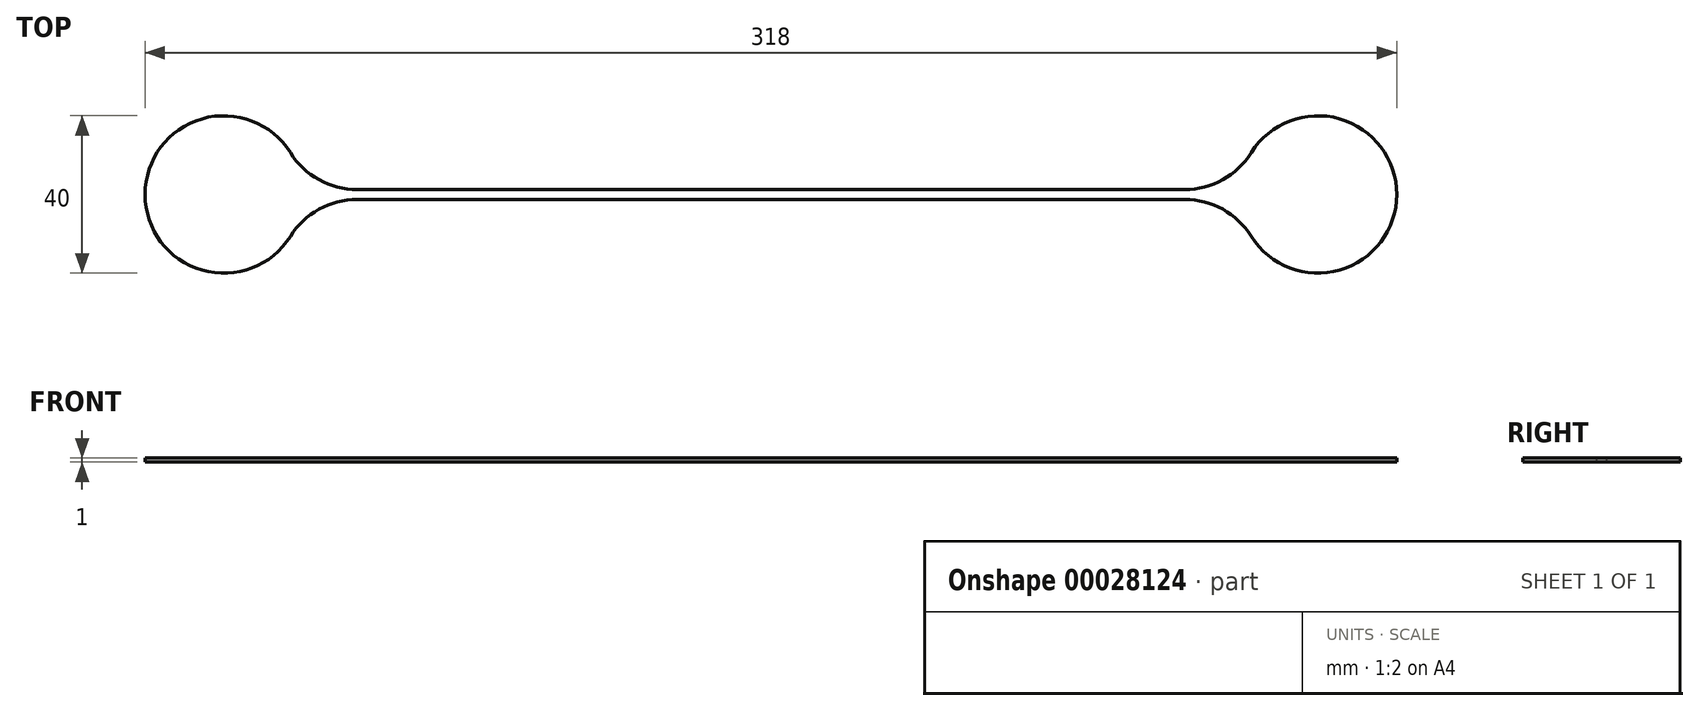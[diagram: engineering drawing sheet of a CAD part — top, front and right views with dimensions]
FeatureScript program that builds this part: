
annotation { "Feature Type Name" : "Feature", "Feature Type Description" : "" }
export const myFeature = defineFeature(function(context is Context, id is Id, definition is map)
    precondition{}
    {
        {
            var Q0;
            Q0=qCreatedBy(makeId("Top.planeOp"),FACE);
            var sketch = newSketch(context, id + "F0", { "sketchPlane" : qUnion([Q0])});
            skLineSegment(sketch, "E0.bottom", {"start": v(-4.06, -40.7) * mm, "end": v(206.17, -40.7) * mm});
            skLineSegment(sketch, "E0.top", {"start": v(-4.06, -43.2) * mm, "end": v(206.17, -43.2) * mm});
            skArc(sketch, "E1", {"start": v(223.1, -52.57) * mm, "mid": v(260.05, -41.94) * mm, "end": v(223.1, -31.32) * mm});
            skArc(sketch, "E2", {"start": v(-21, -31.32) * mm, "mid": v(-57.95, -41.94) * mm, "end": v(-21, -52.57) * mm});
            skPoint(sketch, "E3.end.orphan", {"position": v(-36.68, -43.2) * mm});
            skPoint(sketch, "E3.start.orphan", {"position": v(-39.21, -40.7) * mm});
            skPoint(sketch, "E4.end.orphan", {"position": v(240.05, -40.7) * mm});
            skPoint(sketch, "E4.start.orphan", {"position": v(240.05, -43.2) * mm});
            skPoint(sketch, "E5.visualSharp", {"position": v(-17.98, -40.7) * mm});
            skArc(sketch, "E5.filletArc", {"start": v(-21, -31.32) * mm, "mid": v(-13.74, -38.2) * mm, "end": v(-4.06, -40.7) * mm});
            skPoint(sketch, "E6.visualSharp", {"position": v(-17.98, -43.2) * mm});
            skArc(sketch, "E6.filletArc", {"start": v(-4.06, -43.2) * mm, "mid": v(-13.74, -45.7) * mm, "end": v(-21, -52.57) * mm});
            skPoint(sketch, "E7.visualSharp", {"position": v(220.1, -40.7) * mm});
            skArc(sketch, "E7.filletArc", {"start": v(206.17, -40.7) * mm, "mid": v(215.85, -38.2) * mm, "end": v(223.1, -31.32) * mm});
            skPoint(sketch, "E8.visualSharp", {"position": v(220.1, -43.2) * mm});
            skArc(sketch, "E8.filletArc", {"start": v(223.1, -52.57) * mm, "mid": v(215.85, -45.7) * mm, "end": v(206.17, -43.2) * mm});
            skSolve(sketch);
        }
        {
            var Q0;
            Q0 = qSketchRegion(id + "F0", true);
            extrude(context, id + "F1", {"entities" : qUnion([Q0]), "depth" : 1 * mm});
        }
    });
